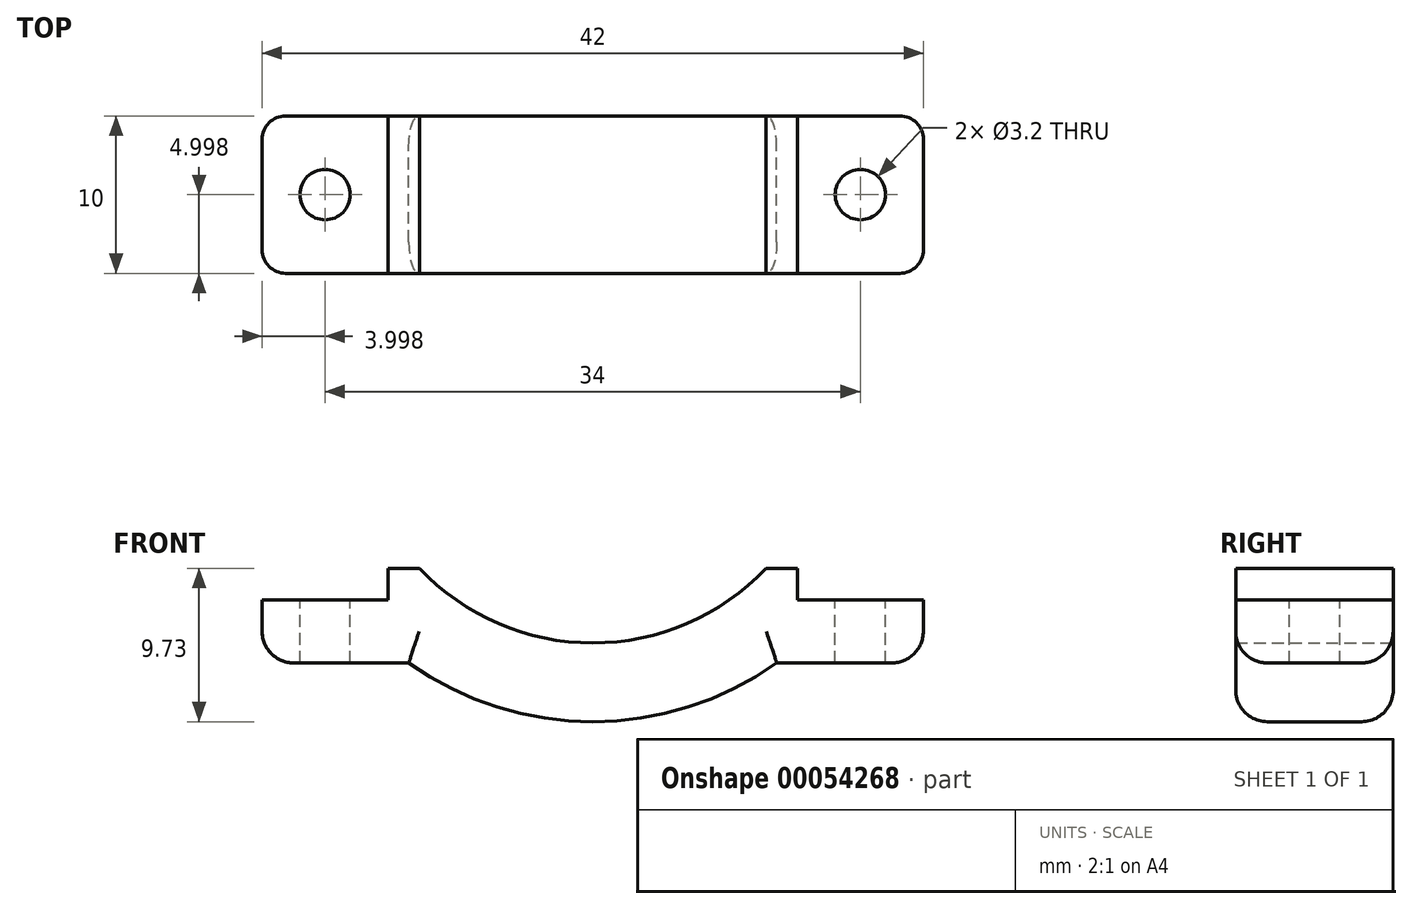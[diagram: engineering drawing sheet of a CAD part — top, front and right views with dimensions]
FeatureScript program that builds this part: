
annotation { "Feature Type Name" : "Feature", "Feature Type Description" : "" }
export const myFeature = defineFeature(function(context is Context, id is Id, definition is map)
    precondition{}
    {
        {
            var Q0;
            Q0=qCreatedBy(makeId("Top.planeOp"),FACE);
            var sketch = newSketch(context, id + "F0", { "sketchPlane" : qUnion([Q0])});
            skLineSegment(sketch, "E0.bottom", {"start": v(-22.47, -1.1) * mm, "end": v(16.53, -1.1) * mm});
            skLineSegment(sketch, "E0.top", {"start": v(-22.47, -11.1) * mm, "end": v(16.53, -11.1) * mm});
            skLineSegment(sketch, "E0.left", {"start": v(-23.97, -2.6) * mm, "end": v(-23.97, -9.6) * mm});
            skLineSegment(sketch, "E0.right", {"start": v(18.03, -2.6) * mm, "end": v(18.03, -9.6) * mm});
            skPoint(sketch, "E1.visualSharp", {"position": v(-23.97, -1.1) * mm});
            skArc(sketch, "E1.filletArc", {"start": v(-22.47, -1.1) * mm, "mid": v(-23.53, -1.54) * mm, "end": v(-23.97, -2.6) * mm});
            skPoint(sketch, "E2.visualSharp", {"position": v(-23.97, -11.1) * mm});
            skArc(sketch, "E2.filletArc", {"start": v(-23.97, -9.6) * mm, "mid": v(-23.53, -10.66) * mm, "end": v(-22.47, -11.1) * mm});
            skPoint(sketch, "E3.visualSharp", {"position": v(18.03, -1.1) * mm});
            skArc(sketch, "E3.filletArc", {"start": v(18.03, -2.6) * mm, "mid": v(17.59, -1.54) * mm, "end": v(16.53, -1.1) * mm});
            skPoint(sketch, "E4.visualSharp", {"position": v(18.03, -11.1) * mm});
            skArc(sketch, "E4.filletArc", {"start": v(16.53, -11.1) * mm, "mid": v(17.59, -10.66) * mm, "end": v(18.03, -9.6) * mm});
            skLineSegment(sketch, "E5.0", {"start": v(10.03, -2.6) * mm, "end": v(10.03, -9.6) * mm, "construction": true});
            skLineSegment(sketch, "E6.0", {"start": v(-15.97, -2.6) * mm, "end": v(-15.97, -9.6) * mm, "construction": true});
            skLineSegment(sketch, "E7", {"start": v(-15.97, -6.1) * mm, "end": v(-23.97, -6.1) * mm, "construction": true});
            skLineSegment(sketch, "E8", {"start": v(-23.97, -6.1) * mm, "end": v(10.03, -6.1) * mm, "construction": true});
            skLineSegment(sketch, "E9", {"start": v(10.03, -6.1) * mm, "end": v(18.03, -6.1) * mm, "construction": true});
            skCircle(sketch, "E10", {"center": v(-19.97, -6.1) * mm, "radius": 1.6 * mm});
            skCircle(sketch, "E11", {"center": v(14.03, -6.1) * mm, "radius": 1.6 * mm});
            skLineSegment(sketch, "E12", {"start": v(-15.97, -1.1) * mm, "end": v(-15.97, -11.1) * mm});
            skLineSegment(sketch, "E13", {"start": v(10.03, -11.1) * mm, "end": v(10.03, -1.1) * mm});
            skSolve(sketch);
        }
        {
            var Q0;
            Q0=makeQuery(id+"F0.imprint","IMPRINT",FACE,{"disambiguationData":[TD([[makeQuery(id+"F0.imprint","IMPRINT",EDGE,{"derivedFrom":sQuery(id+"F0.wireOp",EDGE,"E0.right")}),-1.0]])]});
            var Q1;
            {var subQ0=sQuery(id+"F0.wireOp",EDGE,"E12");Q1=makeQuery(id+"F0.imprint","IMPRINT",FACE,{"disambiguationData":[TD([[makeQuery(id+"F0.imprint","IMPRINT",EDGE,{"derivedFrom":subQ0}),1.0]])]});}
            var Q2;
            Q2=makeQuery(id+"F0.imprint","IMPRINT",FACE,{"disambiguationData":[TD([[makeQuery(id+"F0.imprint","IMPRINT",EDGE,{"derivedFrom":sQuery(id+"F0.wireOp",EDGE,"E0.left")}),1.0]])]});
            extrude(context, id + "F1", {"entities" : qUnion([Q0, Q1, Q2]), "oppositeDirection" : true, "depth" : 4 * mm});
        }
        {
            var Q0;
            {var subQ0=sQuery(id+"F0.wireOp",EDGE,"E12");Q0=makeQuery(id+"F0.imprint","IMPRINT",FACE,{"disambiguationData":[TD([[makeQuery(id+"F0.imprint","IMPRINT",EDGE,{"derivedFrom":subQ0}),1.0]])]});}
            extrude(context, id + "F2", {"entities" : qUnion([Q0]), "operationType" : NewBodyOperationType.ADD, "depth" : 2 * mm});
        }
        {
            var Q0;
            {var subQ0=sQuery(id+"F0.wireOp",EDGE,"E0.bottom");Q0=makeQuery(id+"F2.boolean.opBoolean","MERGE",FACE,{"derivedFrom":[makeQuery(id+"F1.opExtrude","SWEPT_FACE",FACE,{"disambiguationData":[OSD([subQ0])]}),makeQuery(id+"F2.opExtrude","SWEPT_FACE",FACE,{"disambiguationData":[OSD([subQ0])]})]});}
            var sketch = newSketch(context, id + "F3", { "sketchPlane" : qUnion([Q0])});
            skLineSegment(sketch, "E14.0.0", {"start": v(22.47, 0) * mm, "end": v(15.97, 0) * mm});
            skLineSegment(sketch, "E14.0.1", {"start": v(15.97, 0) * mm, "end": v(15.97, 2) * mm});
            skLineSegment(sketch, "E14.0.2", {"start": v(15.97, 2) * mm, "end": v(-10.03, 2) * mm});
            skLineSegment(sketch, "E14.0.3", {"start": v(-10.03, 2) * mm, "end": v(-10.03, 0) * mm});
            skLineSegment(sketch, "E14.0.4", {"start": v(-10.03, 0) * mm, "end": v(-16.53, 0) * mm});
            skLineSegment(sketch, "E14.0.5", {"start": v(-16.53, 0) * mm, "end": v(-16.53, -4) * mm});
            skLineSegment(sketch, "E14.0.6", {"start": v(-16.53, -4) * mm, "end": v(22.47, -4) * mm});
            skLineSegment(sketch, "E14.0.7", {"start": v(22.47, -4) * mm, "end": v(22.47, 0) * mm});
            skLineSegment(sketch, "E15.0", {"start": v(13.97, 0) * mm, "end": v(13.97, 2) * mm, "construction": true});
            skLineSegment(sketch, "E16.0", {"start": v(-8.03, 2) * mm, "end": v(-8.03, 0) * mm, "construction": true});
            skArc(sketch, "E17", {"start": v(-8.03, 2) * mm, "mid": v(2.97, -2.73) * mm, "end": v(13.97, 2) * mm});
            skArc(sketch, "E18.0", {"start": v(-11.66, -1.44) * mm, "mid": v(2.97, -7.73) * mm, "end": v(17.6, -1.44) * mm});
            skSolve(sketch);
        }
        {
            var Q0;
            {var subQ0=sQuery(id+"F3.wireOp",EDGE,"E17");Q0=makeQuery(id+"F3.imprint","IMPRINT",FACE,{"disambiguationData":[TD([[makeQuery(id+"F3.imprint","IMPRINT",EDGE,{"derivedFrom":subQ0}),1.0]])]});}
            var Q1;
            {var subQ0=sQuery(id+"F0.wireOp",EDGE,"E0.top");Q1=makeQuery(id+"F2.boolean.opBoolean","MERGE",FACE,{"derivedFrom":[makeQuery(id+"F1.opExtrude","SWEPT_FACE",FACE,{"disambiguationData":[OSD([subQ0])]}),makeQuery(id+"F2.opExtrude","SWEPT_FACE",FACE,{"disambiguationData":[OSD([subQ0])]})]});}
            extrude(context, id + "F4", {"entities" : qUnion([Q0]), "operationType" : NewBodyOperationType.REMOVE, "endBound" : BoundingType.UP_TO_SURFACE, "oppositeDirection" : true, "endBoundEntityFace" : qUnion([Q1]), "depth" : 25 * mm});
        }
        {
            var Q0;
            {var subQ0=sQuery(id+"F3.wireOp",EDGE,"E18.0");var subQ1=sQuery(id+"F3.wireOp",EDGE,"E14.0.6");var subQ2=makeQuery(id+"F3.imprint","INTERSECT",VERTEX,{"disambiguationData":[OD(0.0)],"derivedFrom":[subQ1,subQ0]});Q0=makeQuery(id+"F3.imprint","IMPRINT",FACE,{"disambiguationData":[TD([[makeQuery(id+"F3.imprint","IMPRINT",EDGE,{"disambiguationData":[TD([[subQ2,-1.0]])],"derivedFrom":subQ1}),1.0]])]});}
            extrude(context, id + "F5", {"entities" : qUnion([Q0]), "operationType" : NewBodyOperationType.ADD, "oppositeDirection" : true, "depth" : 10 * mm});
        }
        {
            var Q0;
            Q0=makeQuery(id+"F5.opExtrude","CAP_EDGE",EDGE,{"disambiguationData":[OSD([sQuery(id+"F3.wireOp",EDGE,"E18.0")])],"isStart":true});
            var Q1;
            Q1=makeQuery(id+"F5.opExtrude","CAP_EDGE",EDGE,{"disambiguationData":[OSD([sQuery(id+"F3.wireOp",EDGE,"E18.0")])],"isStart":false});
            var Q2;
            Q2=makeQuery(id+"F4.boolean.opBoolean","COPY",EDGE,{"derivedFrom":makeQuery(id+"F4.opExtrude","CAP_EDGE",EDGE,{"disambiguationData":[OSD([sQuery(id+"F3.wireOp",EDGE,"E17")])],"isStart":true})});
            var Q3;
            Q3=makeQuery(id+"F4.boolean.opBoolean","COPY",EDGE,{"derivedFrom":makeQuery(id+"F4.opExtrude","CAP_EDGE",EDGE,{"disambiguationData":[OSD([sQuery(id+"F3.wireOp",EDGE,"E17")])],"isStart":false})});
            var Q4;
            {var subQ0=sQuery(id+"F0.wireOp",EDGE,"E0.top");var subQ2=sQuery(id+"F0.wireOp",EDGE,"E4.filletArc");Q4=makeQuery(id+"F5.boolean.opBoolean","SPLIT",EDGE,{"disambiguationData":[TD([makeQuery(id+"F1.opExtrude","SWEPT_FACE",FACE,{"disambiguationData":[OSD([subQ2])]})])],"derivedFrom":makeQuery(id+"F1.opExtrude","CAP_EDGE",EDGE,{"disambiguationData":[OSD([subQ0])],"isStart":false})});}
            var Q5;
            {var subQ0=sQuery(id+"F0.wireOp",EDGE,"E0.top");var subQ2=sQuery(id+"F0.wireOp",EDGE,"E2.filletArc");Q5=makeQuery(id+"F5.boolean.opBoolean","SPLIT",EDGE,{"disambiguationData":[TD([makeQuery(id+"F1.opExtrude","SWEPT_FACE",FACE,{"disambiguationData":[OSD([subQ2])]})])],"derivedFrom":makeQuery(id+"F1.opExtrude","CAP_EDGE",EDGE,{"disambiguationData":[OSD([subQ0])],"isStart":false})});}
            fillet(context, id + "F6", {"entities" : qUnion([Q0, Q1, Q2, Q3, Q4, Q5]), "radius" : 2 * mm, "tangentPropagation" : true, "allowEdgeOverflow" : false});
        }
    });
